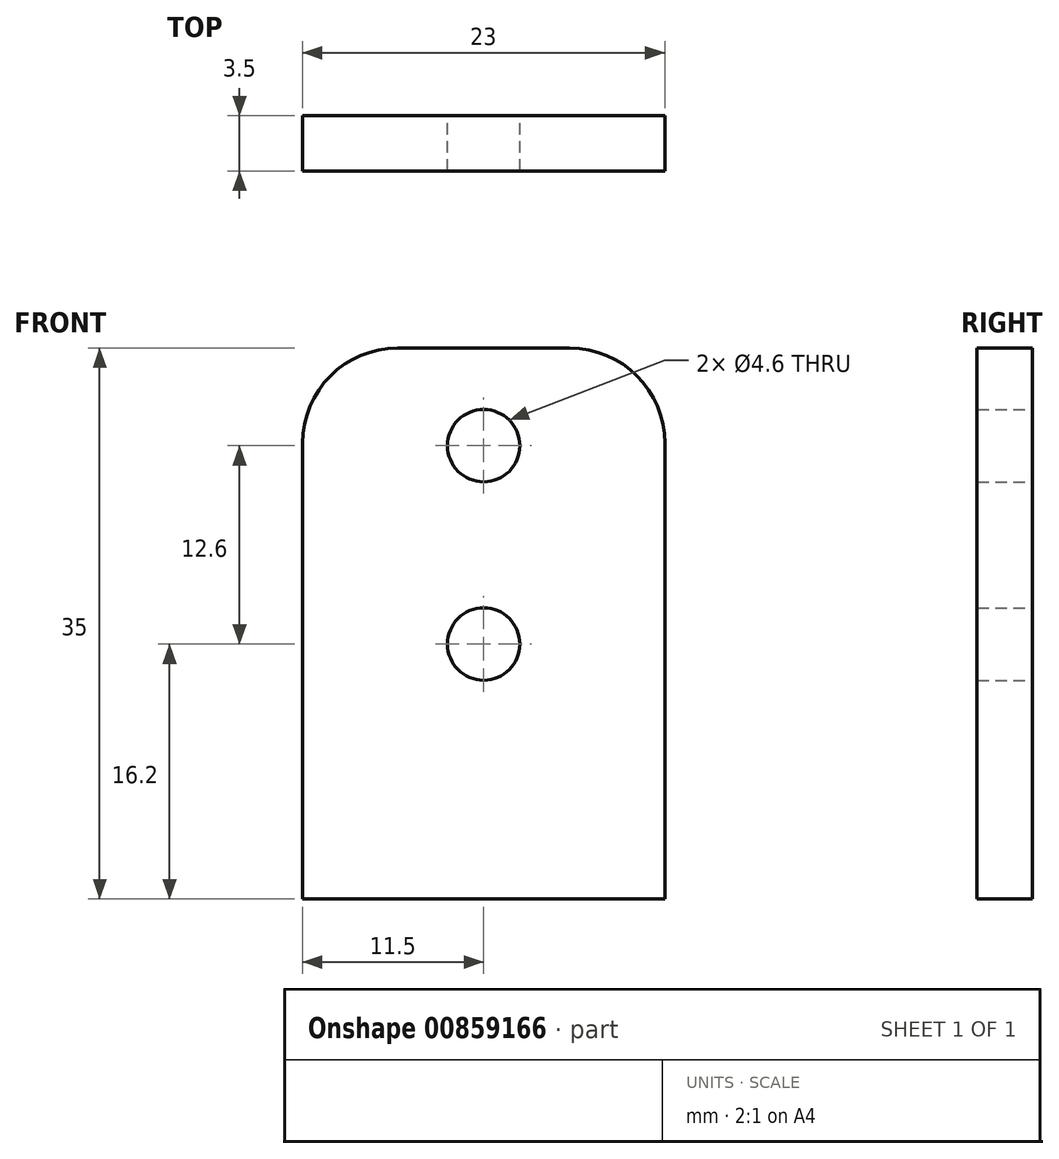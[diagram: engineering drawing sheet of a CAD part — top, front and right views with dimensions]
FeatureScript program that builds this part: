
annotation { "Feature Type Name" : "Feature", "Feature Type Description" : "" }
export const myFeature = defineFeature(function(context is Context, id is Id, definition is map)
    precondition{}
    {
        {
            var Q0;
            Q0=qCreatedBy(makeId("Front.planeOp"),FACE);
            var sketch = newSketch(context, id + "F0", { "sketchPlane" : qUnion([Q0])});
            skLineSegment(sketch, "E0.bottom", {"start": v(0, 0) * mm, "end": v(23, 0) * mm});
            skLineSegment(sketch, "E0.top", {"start": v(6.04, 35) * mm, "end": v(16.96, 35) * mm});
            skLineSegment(sketch, "E0.left", {"start": v(0, 0) * mm, "end": v(0, 28.96) * mm});
            skLineSegment(sketch, "E0.right", {"start": v(23, 0) * mm, "end": v(23, 28.96) * mm});
            skLineSegment(sketch, "E1", {"start": v(0, 0) * mm, "end": v(0, 6.5) * mm});
            skLineSegment(sketch, "E2", {"start": v(0, 6.5) * mm, "end": v(-10.09, 0) * mm});
            skLineSegment(sketch, "E3", {"start": v(-10.09, 0) * mm, "end": v(0, 0) * mm});
            skLineSegment(sketch, "E4", {"start": v(23, 0) * mm, "end": v(23, 15.5) * mm});
            skLineSegment(sketch, "E5", {"start": v(23, 15.5) * mm, "end": v(32.99, 0) * mm});
            skLineSegment(sketch, "E6", {"start": v(32.99, 0) * mm, "end": v(23, 0) * mm});
            skLineSegment(sketch, "E7", {"start": v(11.5, 35) * mm, "end": v(11.5, 31.1) * mm});
            skLineSegment(sketch, "E8", {"start": v(11.5, 31.1) * mm, "end": v(11.5, 28.8) * mm});
            skCircle(sketch, "E9", {"center": v(11.5, 28.8) * mm, "radius": 2.3 * mm});
            skLineSegment(sketch, "E10", {"start": v(11.5, 28.8) * mm, "end": v(11.5, 26.5) * mm});
            skLineSegment(sketch, "E11", {"start": v(11.5, 26.5) * mm, "end": v(11.5, 18.5) * mm});
            skLineSegment(sketch, "E12", {"start": v(11.5, 18.5) * mm, "end": v(11.5, 16.2) * mm});
            skCircle(sketch, "E13", {"center": v(11.5, 16.2) * mm, "radius": 2.3 * mm});
            skPoint(sketch, "E14.visualSharp", {"position": v(23, 35) * mm});
            skArc(sketch, "E14.filletArc", {"start": v(23, 28.96) * mm, "mid": v(21.23, 33.23) * mm, "end": v(16.96, 35) * mm});
            skPoint(sketch, "E15.visualSharp", {"position": v(0, 35) * mm});
            skArc(sketch, "E15.filletArc", {"start": v(6.04, 35) * mm, "mid": v(1.77, 33.23) * mm, "end": v(0, 28.96) * mm});
            skSolve(sketch);
        }
        {
            var Q0;
            Q0=makeQuery(id+"F0.imprint","IMPRINT",FACE,{"disambiguationData":[TD([[makeQuery(id+"F0.imprint","IMPRINT",EDGE,{"derivedFrom":sQuery(id+"F0.wireOp",EDGE,"E0.bottom")}),1.0]])]});
            var Q1;
            Q1=makeQuery(id+"F0.imprint","IMPRINT",FACE,{"disambiguationData":[TD([[makeQuery(id+"F0.imprint","IMPRINT",EDGE,{"derivedFrom":sQuery(id+"F0.wireOp",EDGE,"E4")}),-1.0]])]});
            var Q2;
            Q2=makeQuery(id+"F0.imprint","IMPRINT",FACE,{"disambiguationData":[TD([[makeQuery(id+"F0.imprint","IMPRINT",EDGE,{"derivedFrom":sQuery(id+"F0.wireOp",EDGE,"E1")}),1.0]])]});
            extrude(context, id + "F1", {"entities" : qUnion([Q0, Q1, Q2]), "depth" : 3.5 * mm, "offsetDistance" : 25 * mm});
        }
    });
